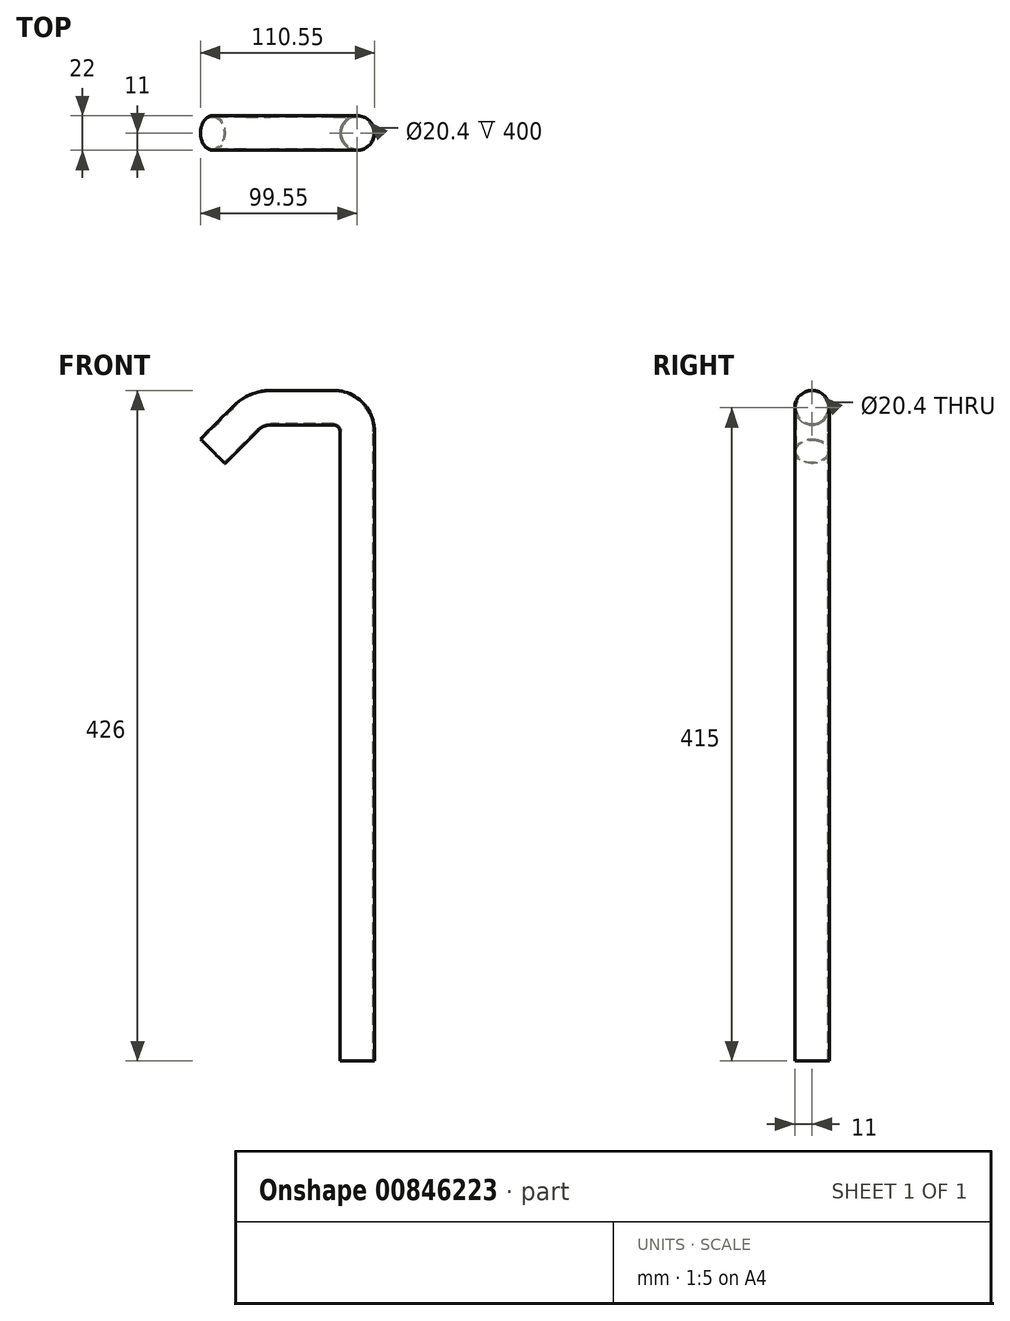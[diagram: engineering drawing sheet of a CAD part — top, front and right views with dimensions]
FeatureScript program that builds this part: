
annotation { "Feature Type Name" : "Feature", "Feature Type Description" : "" }
export const myFeature = defineFeature(function(context is Context, id is Id, definition is map)
    precondition{}
    {
        {
            var Q0;
            Q0=qCreatedBy(makeId("Front.planeOp"),FACE);
            var sketch = newSketch(context, id + "F0", { "sketchPlane" : qUnion([Q0])});
            skLineSegment(sketch, "E0", {"start": v(0, 0) * mm, "end": v(0, 400) * mm});
            skArc(sketch, "E1", {"start": v(0, 400) * mm, "mid": v(-4.4, 410.6) * mm, "end": v(-15, 415) * mm});
            skLineSegment(sketch, "E2", {"start": v(-15, 415) * mm, "end": v(-55, 415) * mm});
            skArc(sketch, "E3", {"start": v(-55, 415) * mm, "mid": v(-63.42, 413.33) * mm, "end": v(-70.56, 408.56) * mm});
            skLineSegment(sketch, "E4", {"start": v(-70.56, 408.56) * mm, "end": v(-91.77, 387.34) * mm});
            skSolve(sketch);
        }
        {
            var Q0;
            Q0=qCreatedBy(makeId("Top.planeOp"),FACE);
            var sketch = newSketch(context, id + "F1", { "sketchPlane" : qUnion([Q0])});
            skCircle(sketch, "E5", {"center": v(0, 0) * mm, "radius": 11 * mm});
            skSolve(sketch);
        }
        {
            var Q0;
            Q0 = qSketchRegion(id + "F1", true);
            var Q1;
            Q1 = qConstructionFilter(qBodyType(qCreatedBy(id + "F0" ,EDGE), BodyType.WIRE), ConstructionObject.NO);
            sweep(context, id + "F2", {"profiles" : qUnion([Q0]), "path" : qUnion([Q1])});
        }
        {
            var Q0;
            Q0=makeQuery(id+"F2.opSweep","CAP_FACE",FACE,{"disambiguationData":[OSD([sQuery(id+"F0.wireOp",VERTEX,"E4.end"),sQuery(id+"F1.wireOp",EDGE,"E5")])],"isStart":false});
            var Q1;
            Q1=makeQuery(id+"F2.opSweep","CAP_FACE",FACE,{"disambiguationData":[OSD([sQuery(id+"F0.wireOp",VERTEX,"E0.start"),sQuery(id+"F1.wireOp",EDGE,"E5")])],"isStart":true});
            shell(context, id + "F3", {"entities" : qUnion([Q0, Q1]), "thickness" : 0.8 * mm});
        }
    });
